FCSTD DOCUMENT  (FreeCAD 0.20R29177 +426 (Git))
Label: PortalRotatorSketch
License: All rights reserved
LicenseURL: http://en.wikipedia.org/wiki/All_rights_reserved
objects: PartDesign::CoordinateSystem×2, Sketcher::SketchObject×1, PartDesign::Body×1
note: 4 computed .brp shape members not serialized (recipe doc carries the construction recipe); baked Part::Feature solids carry a one-line shape summary decoded from their .brp
EXTERNAL_REF file=assembly4.FCStd obj=Variables

FEATURE [PartDesign::CoordinateSystem] LCS_Origin
  AttacherType = Attacher::AttachEngine3D
  MapMode = 2
  Support = -> [X_Axis]
FEATURE [Sketcher::SketchObject] Sketch
  FullyConstrained = true
  MapMode = 5
  Support = -> [XY_Plane]
  expr: Constraints[0] = assembly4#Variables.PortalRotatorDeg
  sketch-geometry (1):
    g0: LineSegment StartX=0 StartY=0 StartZ=0 EndX=6.8404 EndY=18.7939 EndZ=0
  constraints (3):
    c: Angle(g0,g-1) = -1.22173
    c: Coincident(g0,g-1)
    c: Distance(g0) = 20
FEATURE [PartDesign::CoordinateSystem] LCSRotator
  AttacherType = Attacher::AttachEngine3D
  MapMode = 7
  Placement = pos=(0,0,0) rot=(0.970288,-0.171088,-0.171088;1.60095rad)
  Support = -> [Sketch]
FEATURE [PartDesign::Body] PortalRotatorBody
  Group = -> [LCS_Origin,Sketch,LCSRotator]
  Origin = -> Origin
